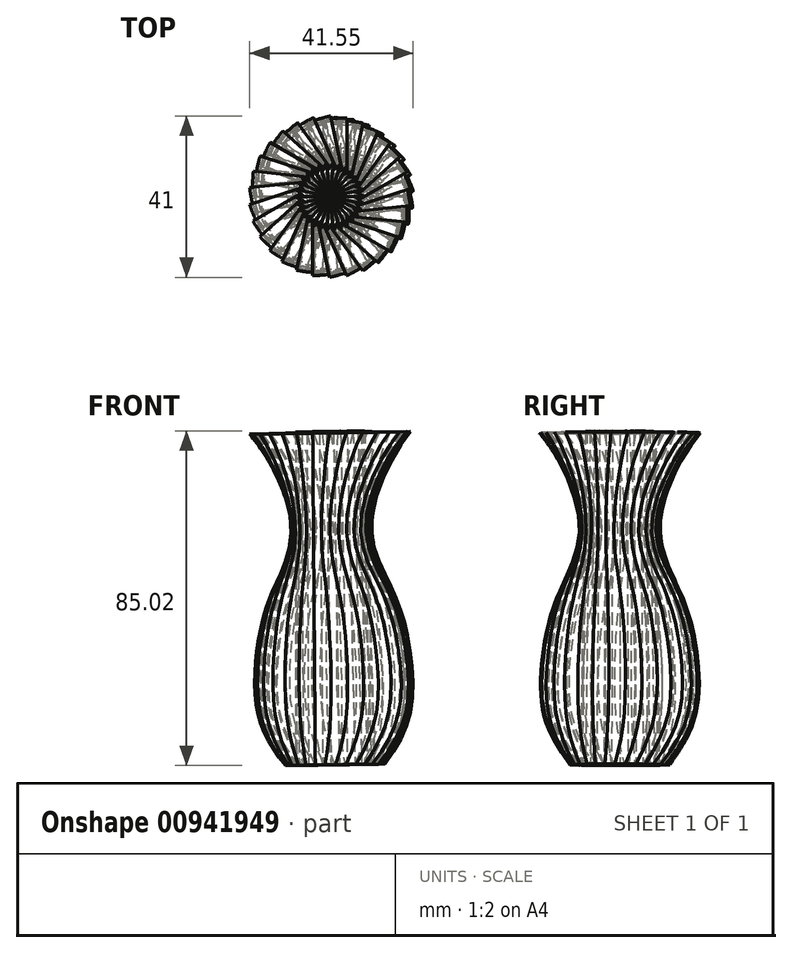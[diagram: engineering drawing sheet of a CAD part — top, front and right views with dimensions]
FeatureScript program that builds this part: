
annotation { "Feature Type Name" : "Feature", "Feature Type Description" : "" }
export const myFeature = defineFeature(function(context is Context, id is Id, definition is map)
    precondition{}
    {
        {
            var Q0;
            Q0=qCreatedBy(makeId("Front.planeOp"),FACE);
            var sketch = newSketch(context, id + "F0", { "sketchPlane" : qUnion([Q0])});
            skLineSegment(sketch, "E0", {"start": v(0, 39.27) * mm, "end": v(0, -45.16) * mm});
            skLineSegment(sketch, "E1", {"start": v(0, -45.16) * mm, "end": v(20.34, -45.16) * mm});
            skLineSegment(sketch, "E2", {"start": v(0, 39.27) * mm, "end": v(27.62, 39.27) * mm});
            skPoint(sketch, "E3.endSnap0", {"position": v(10.17, -45.16) * mm});
            skFitSpline(sketch, "E4", {"points": [v(27.62, 39.27) * mm, v(17.15, 15.94) * mm, v(22.23, 0) * mm, v(26.53, -12.2) * mm, v(27.62, -30.65) * mm, v(20.34, -45.16) * mm], "startDerivative": vector(-55.1, -63.1) * mm, "endDerivative": vector(-59.66, -74.58) * mm});
            skLineSegment(sketch, "E5", {"start": v(9.38, -0.88) * mm, "end": v(9.7, -21.6) * mm});
            skSolve(sketch);
        }
        {
            var Q0;
            {var subQ0=sQuery(id+"F0.wireOp",EDGE,"E0");Q0=makeQuery(id+"F0.imprint","IMPRINT",FACE,{"disambiguationData":[TD([[makeQuery(id+"F0.imprint","IMPRINT",EDGE,{"derivedFrom":subQ0}),1.0]])]});}
            var Q1;
            Q1=sQuery(id+"F0.wireOp",EDGE,"E0");
            revolve(context, id + "F1", {"entities" : qUnion([Q0]), "axis" : qUnion([Q1]), "revolveType" : RevolveType.ONE_DIRECTION, "angle" : 30 * degree});
        }
        {
            var Q0;
            Q0=makeQuery(id+"F1.opRevolve","SWEPT_BODY",BODY,{"disambiguationData":[OSD([sQuery(id+"F0.wireOp",EDGE,"E0"),sQuery(id+"F0.wireOp",EDGE,"E1"),sQuery(id+"F0.wireOp",EDGE,"E2"),sQuery(id+"F0.wireOp",EDGE,"e89406fa-a3c8-4e77-b4de-1d4cb888b24e")])]});
            var Q1;
            Q1=sQuery(id+"F0.wireOp",EDGE,"E5");
            circularPattern(context, id + "F2", {"entities" : qUnion([Q0]), "axis" : qUnion([Q1]), "angle" : 360 * degree, "instanceCount" : 30, "equalSpace" : true});
        }
        {
            var Q0;
            Q0=qCreatedBy(makeId("Front.planeOp"),FACE);
            var sketch = newSketch(context, id + "F3", { "sketchPlane" : qUnion([Q0])});
            skFitSpline(sketch, "E6", {"points": [v(23.35, -12.63) * mm, v(35.16, -15.97) * mm, v(23.6, -30.6) * mm, v(23.35, -12.63) * mm]});
            skSolve(sketch);
        }
        {
            var Q0;
            Q0=sQuery(id+"F3.wireOp",EDGE,"E6");
            var Q1;
            Q1=sQuery(id+"F0.wireOp",EDGE,"E5");
            revolve(context, id + "F4", {"bodyType" : ToolBodyType.SURFACE, "surfaceEntities" : qUnion([Q0]), "axis" : qUnion([Q1]), "revolveType" : RevolveType.FULL});
        }
    });
